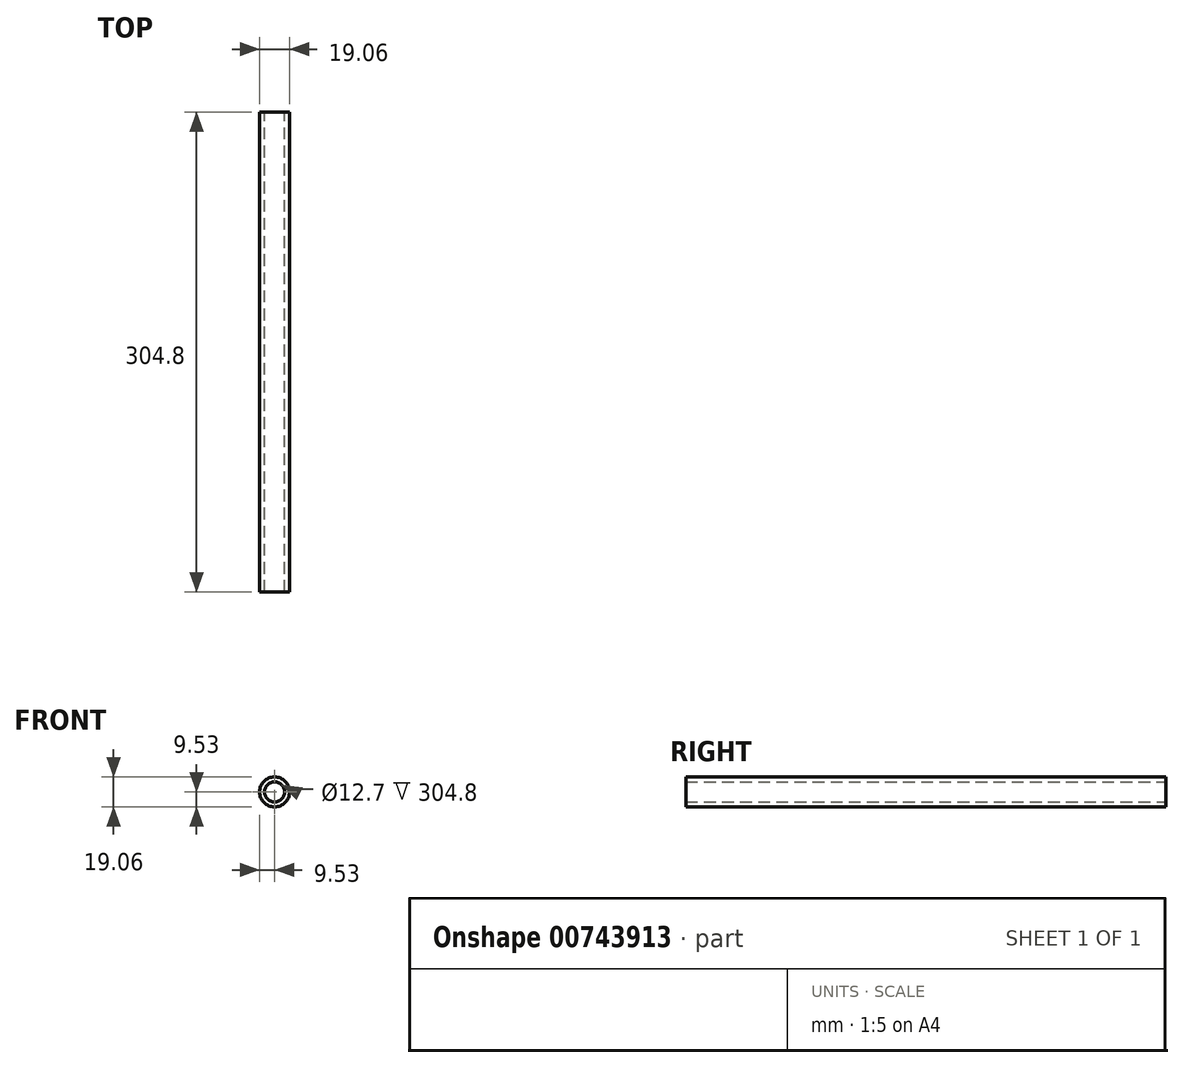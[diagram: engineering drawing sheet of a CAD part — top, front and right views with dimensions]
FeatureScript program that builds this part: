
annotation { "Feature Type Name" : "Feature", "Feature Type Description" : "" }
export const myFeature = defineFeature(function(context is Context, id is Id, definition is map)
    precondition{}
    {
        {
            var Q0;
            Q0=qCreatedBy(makeId("Front.planeOp"),FACE);
            var sketch = newSketch(context, id + "F0", { "sketchPlane" : qUnion([Q0])});
            skCircle(sketch, "E0", {"center": v(0, 0) * mm, "radius": 9.53 * mm});
            skCircle(sketch, "E1", {"center": v(0, 0) * mm, "radius": 6.35 * mm});
            skSolve(sketch);
        }
        {
            var Q0;
            Q0 = qSketchRegion(id + "F0", true);
            extrude(context, id + "F1", {"entities" : qUnion([Q0]), "depth" : 304.8 * mm, "offsetDistance" : 25.4 * mm});
        }
    });
